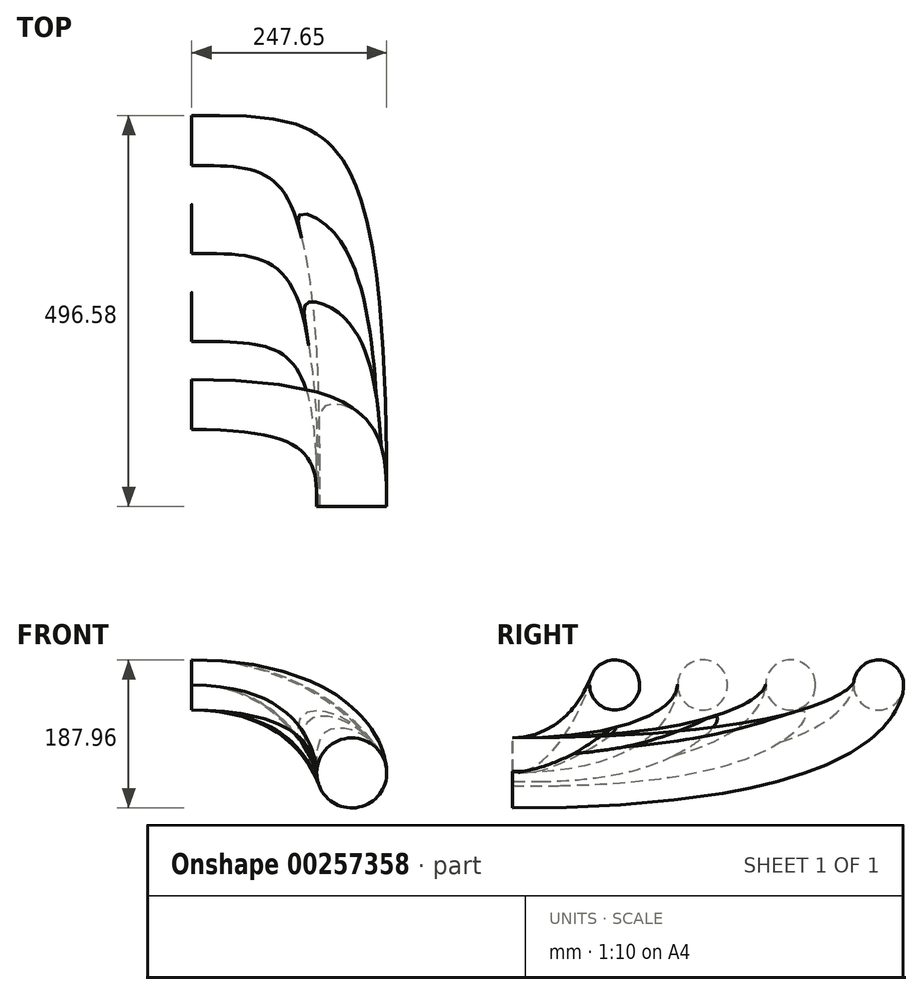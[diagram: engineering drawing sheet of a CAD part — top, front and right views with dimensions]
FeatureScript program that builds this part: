
annotation { "Feature Type Name" : "Feature", "Feature Type Description" : "" }
export const myFeature = defineFeature(function(context is Context, id is Id, definition is map)
    precondition{}
    {
        {
            var Q0;
            Q0=qCreatedBy(makeId("Right.planeOp"),FACE);
            cPlane(context, id + "F0", {"entities" : qUnion([Q0]), "cplaneType" : CPlaneType.OFFSET, "offset" : 203.2 * mm, "oppositeDirection" : true, "width" : 152.4 * mm, "height" : 152.4 * mm});
        }
        {
            var Q0;
            Q0=qCreatedBy(makeId("Top.planeOp"),FACE);
            cPlane(context, id + "F1", {"entities" : qUnion([Q0]), "cplaneType" : CPlaneType.OFFSET, "offset" : 111.76 * mm, "width" : 152.4 * mm, "height" : 152.4 * mm});
        }
        {
            var Q0;
            Q0=qCreatedBy(makeId("Front.planeOp"),FACE);
            var sketch = newSketch(context, id + "F2", { "sketchPlane" : qUnion([Q0])});
            skCircle(sketch, "E0", {"center": v(0, 0) * mm, "radius": 44.45 * mm});
            skSolve(sketch);
        }
        {
            var Q0;
            Q0=qCreatedBy(id+"F0.planeOp",FACE);
            var sketch = newSketch(context, id + "F3", { "sketchPlane" : qUnion([Q0])});
            skCircle(sketch, "E1", {"center": v(129.54, 111.76) * mm, "radius": 31.75 * mm});
            skCircle(sketch, "E2.1.0.0", {"center": v(241.3, 111.76) * mm, "radius": 31.75 * mm});
            skCircle(sketch, "E2.2.0.0", {"center": v(353.06, 111.76) * mm, "radius": 31.75 * mm});
            skCircle(sketch, "E2.3.0.0", {"center": v(464.82, 111.76) * mm, "radius": 31.75 * mm});
            skLineSegment(sketch, "E2.direction1", {"start": v(129.54, 111.76) * mm, "end": v(241.3, 111.76) * mm, "construction": true});
            skSolve(sketch);
        }
        {
            var Q0;
            Q0=qCreatedBy(id+"F1.planeOp",FACE);
            var sketch = newSketch(context, id + "F4", { "sketchPlane" : qUnion([Q0])});
            skPoint(sketch, "E3.0", {"position": v(-203.2, 129.54) * mm});
            skPoint(sketch, "E4.0", {"position": v(-203.2, 241.3) * mm});
            skPoint(sketch, "E5.0", {"position": v(-203.2, 353.06) * mm});
            skLineSegment(sketch, "E6.0", {"start": v(-203.2, 161.3) * mm, "end": v(-203.2, 97.8) * mm});
            skLineSegment(sketch, "E7.0", {"start": v(-203.2, 273.05) * mm, "end": v(-203.2, 209.55) * mm});
            skLineSegment(sketch, "E8.0", {"start": v(-203.2, 384.81) * mm, "end": v(-203.2, 321.31) * mm});
            skLineSegment(sketch, "E9.0", {"start": v(-203.2, 496.57) * mm, "end": v(-203.2, 433.07) * mm});
            skLineSegment(sketch, "E10", {"start": v(-203.2, 97.8) * mm, "end": v(-177.8, 97.8) * mm});
            skLineSegment(sketch, "E11.0.1.0", {"start": v(-203.2, 209.55) * mm, "end": v(-177.8, 209.55) * mm});
            skLineSegment(sketch, "E11.0.2.0", {"start": v(-203.2, 321.31) * mm, "end": v(-177.8, 321.31) * mm});
            skLineSegment(sketch, "E11.0.3.0", {"start": v(-203.2, 433.07) * mm, "end": v(-177.8, 433.07) * mm});
            skLineSegment(sketch, "E11.direction1", {"start": v(-203.2, 97.8) * mm, "end": v(-177.8, 97.8) * mm, "construction": true});
            skLineSegment(sketch, "E11.direction2", {"start": v(-203.2, 97.8) * mm, "end": v(-203.2, 209.55) * mm, "construction": true});
            skSolve(sketch);
        }
        {
            var Q0;
            Q0=qCreatedBy(makeId("Top.planeOp"),FACE);
            var sketch = newSketch(context, id + "F5", { "sketchPlane" : qUnion([Q0])});
            skLineSegment(sketch, "E12.0", {"start": v(44.45, 0) * mm, "end": v(-44.45, 0) * mm});
            skLineSegment(sketch, "E13", {"start": v(-44.45, 0) * mm, "end": v(-44.45, 25.4) * mm});
            skSolve(sketch);
        }
        {
            var Q0;
            Q0=makeQuery(id+"F2.imprint","IMPRINT",FACE,{"disambiguationData":[TD([[makeQuery(id+"F2.imprint","IMPRINT",EDGE,{"derivedFrom":sQuery(id+"F2.wireOp",EDGE,"E0")}),1.0]])]});
            var Q1;
            Q1=makeQuery(id+"F3.imprint","IMPRINT",FACE,{"disambiguationData":[TD([[makeQuery(id+"F3.imprint","IMPRINT",EDGE,{"derivedFrom":sQuery(id+"F3.wireOp",EDGE,"E1")}),1.0]])]});
            var Q2;
            Q2=sQuery(id+"F4.wireOp",VERTEX,"E6.0.end");
            var Q3;
            Q3=sQuery(id+"F5.wireOp",VERTEX,"E13.start");
            loft(context, id + "F6", {"startCondition" : LoftEndDerivativeType.NORMAL_TO_PROFILE, "startMagnitude" : 1.6, "endCondition" : LoftEndDerivativeType.NORMAL_TO_PROFILE, "endMagnitude" : 2.9, "sheetProfilesArray" : [{ "sheetProfileEntities" : qUnion([Q0]) }, { "sheetProfileEntities" : qUnion([Q1]) }], "matchConnections" : true, "connections" : [{ "connectionEntities" : qUnion([Q2, Q3]), "connectionEdgeQueries" : qUnion([]), "connectionEdgeParameters" : [] }]});
        }
        {
            var Q1;
            Q1=makeQuery(id+"F3.imprint","IMPRINT",FACE,{"disambiguationData":[TD([[makeQuery(id+"F3.imprint","IMPRINT",EDGE,{"derivedFrom":sQuery(id+"F3.wireOp",EDGE,"E2.1.0.0")}),1.0]])]});
            var Q2;
            Q2=makeQuery(id+"F2.imprint","IMPRINT",FACE,{"disambiguationData":[TD([[makeQuery(id+"F2.imprint","IMPRINT",EDGE,{"derivedFrom":sQuery(id+"F2.wireOp",EDGE,"E0")}),1.0]])]});
            var Q3;
            Q3=sQuery(id+"F5.wireOp",VERTEX,"E13.start");
            var Q4;
            Q4=sQuery(id+"F4.wireOp",VERTEX,"E11.0.1.0.start");
            loft(context, id + "F7", {"operationType" : NewBodyOperationType.ADD, "startCondition" : LoftEndDerivativeType.NORMAL_TO_PROFILE, "startMagnitude" : 2.2, "endCondition" : LoftEndDerivativeType.NORMAL_TO_PROFILE, "endMagnitude" : 2.9, "sheetProfilesArray" : [{ "sheetProfileEntities" : qUnion([Q1]) }, { "sheetProfileEntities" : qUnion([Q2]) }], "matchConnections" : true, "connections" : [{ "connectionEntities" : qUnion([Q3, Q4]), "connectionEdgeQueries" : qUnion([]), "connectionEdgeParameters" : [] }]});
        }
        {
            var Q1;
            Q1=makeQuery(id+"F2.imprint","IMPRINT",FACE,{"disambiguationData":[TD([[makeQuery(id+"F2.imprint","IMPRINT",EDGE,{"derivedFrom":sQuery(id+"F2.wireOp",EDGE,"E0")}),1.0]])]});
            var Q2;
            Q2=makeQuery(id+"F3.imprint","IMPRINT",FACE,{"disambiguationData":[TD([[makeQuery(id+"F3.imprint","IMPRINT",EDGE,{"derivedFrom":sQuery(id+"F3.wireOp",EDGE,"E2.2.0.0")}),1.0]])]});
            var Q3;
            Q3=sQuery(id+"F5.wireOp",VERTEX,"E13.start");
            var Q4;
            Q4=sQuery(id+"F4.wireOp",VERTEX,"E11.0.2.0.start");
            loft(context, id + "F8", {"operationType" : NewBodyOperationType.ADD, "startCondition" : LoftEndDerivativeType.NORMAL_TO_PROFILE, "startMagnitude" : 3, "endCondition" : LoftEndDerivativeType.NORMAL_TO_PROFILE, "endMagnitude" : 2, "sheetProfilesArray" : [{ "sheetProfileEntities" : qUnion([Q1]) }, { "sheetProfileEntities" : qUnion([Q2]) }], "matchConnections" : true, "connections" : [{ "connectionEntities" : qUnion([Q3, Q4]), "connectionEdgeQueries" : qUnion([]), "connectionEdgeParameters" : [] }]});
        }
        {
            var Q1;
            Q1=makeQuery(id+"F2.imprint","IMPRINT",FACE,{"disambiguationData":[TD([[makeQuery(id+"F2.imprint","IMPRINT",EDGE,{"derivedFrom":sQuery(id+"F2.wireOp",EDGE,"E0")}),1.0]])]});
            var Q2;
            Q2=makeQuery(id+"F3.imprint","IMPRINT",FACE,{"disambiguationData":[TD([[makeQuery(id+"F3.imprint","IMPRINT",EDGE,{"derivedFrom":sQuery(id+"F3.wireOp",EDGE,"E2.3.0.0")}),1.0]])]});
            var Q3;
            Q3=sQuery(id+"F5.wireOp",VERTEX,"E13.start");
            var Q4;
            Q4=sQuery(id+"F4.wireOp",VERTEX,"E9.0.end");
            loft(context, id + "F9", {"operationType" : NewBodyOperationType.ADD, "startCondition" : LoftEndDerivativeType.NORMAL_TO_PROFILE, "startMagnitude" : 3, "endCondition" : LoftEndDerivativeType.NORMAL_TO_PROFILE, "endMagnitude" : 2, "sheetProfilesArray" : [{ "sheetProfileEntities" : qUnion([Q1]) }, { "sheetProfileEntities" : qUnion([Q2]) }], "matchConnections" : true, "connections" : [{ "connectionEntities" : qUnion([Q3, Q4]), "connectionEdgeQueries" : qUnion([]), "connectionEdgeParameters" : [] }]});
        }
    });
